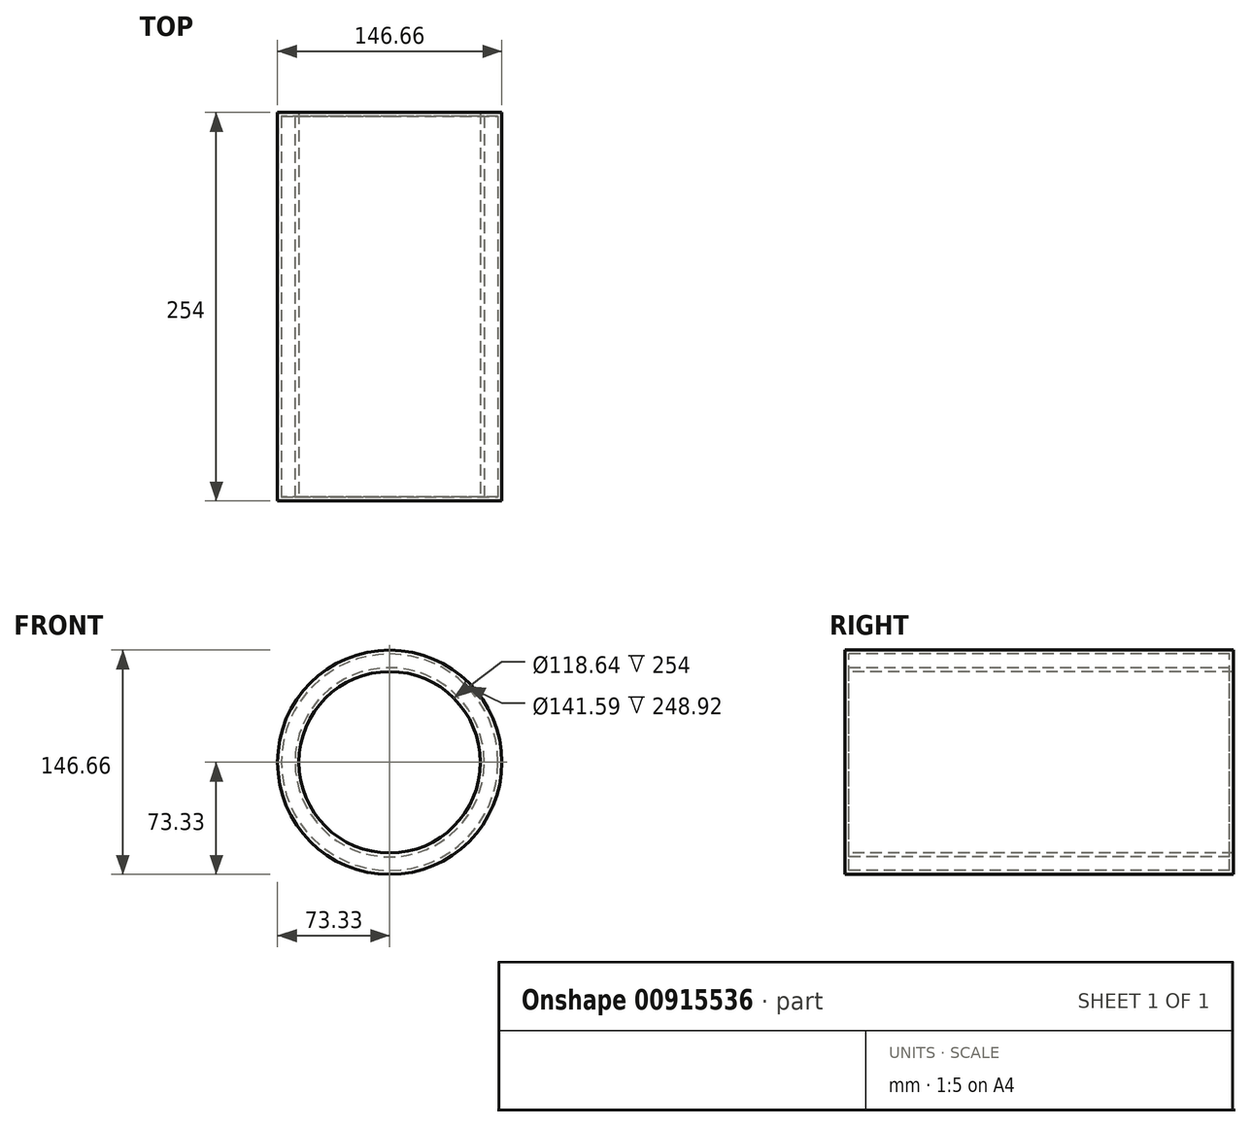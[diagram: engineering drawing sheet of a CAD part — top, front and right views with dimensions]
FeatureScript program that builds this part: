
annotation { "Feature Type Name" : "Feature", "Feature Type Description" : "" }
export const myFeature = defineFeature(function(context is Context, id is Id, definition is map)
    precondition{}
    {
        {
            var Q0;
            Q0=qCreatedBy(makeId("Front.planeOp"),FACE);
            var sketch = newSketch(context, id + "F0", { "sketchPlane" : qUnion([Q0])});
            skCircle(sketch, "E0", {"center": v(0, 0) * mm, "radius": 73.33 * mm});
            skCircle(sketch, "E1", {"center": v(0, 0) * mm, "radius": 59.32 * mm});
            skSolve(sketch);
        }
        {
            var Q0;
            Q0 = qSketchRegion(id + "F0", true);
            extrude(context, id + "F1", {"entities" : qUnion([Q0]), "oppositeDirection" : true, "depth" : 254 * mm, "offsetDistance" : 25.4 * mm});
        }
        {
            var Q0;
            Q0=makeQuery(id+"F1.opExtrude","SWEPT_FACE",FACE,{"disambiguationData":[OSD([sQuery(id+"F0.wireOp",EDGE,"E1")])]});
            var Q1;
            Q1=makeQuery(id+"F1.opExtrude","SWEPT_BODY",BODY,{"disambiguationData":[OSD([sQuery(id+"F0.wireOp",EDGE,"E0"),sQuery(id+"F0.wireOp",EDGE,"E1")])]});
            shell(context, id + "F2", {"isHollow" : true, "entities" : qUnion([Q0]), "parts" : qUnion([Q1]), "thickness" : 2.54 * mm});
        }
    });
